# Revit family: NAU_Naughtone_Stng_Pullman1
name_source: partatom
category: Furniture
revit_build: Autodesk Revit 2018 (Build: 20170223_1515(x64)
units: mm (PartAtom-declared; Revit-internal decimal feet)

## family parameters
Always vertical = Yes
Cut with Voids When Loaded = No
OmniClass Number = 23.40.20.00
OmniClass Title = General Furniture and Specialties
Room Calculation Point = No
Shared = Yes
Work Plane-Based = No

## types (4) — shared parameters
AccessibilityPerformance = Table Top
Assembly Code = E2020200
AssetType = Movable
BIMObjectName = NAU_Naughtone_Seating_Pullman
Category = Pr_40_50_31 : Furniture booths
Color = Various
DurationUnit = year
Finish = Fabric upholstery
IfcExportAs = IfcFurnishingElementType
IfcExportType = BOOTH
Keynote = Pr_40_50_31
MainColor = Various
ManufacturerAddress = Knaresborough Tech Park, Manse Lane, Knaresborough, HG5 8LF
ManufacturerName = Naughtone
ManufacturerURL = www.naughtone.com
Material = Fabric, plywood frame, foam, steel/wooden legs, wooden table top
NBSDescription = Seating
NBSReference = 45-35-72/352
Name = Seating_Pullman_Naughtone
NominalHeight = 1300 mm  [stored 4.26509 ft]
ProductInformation = www.naughtone.com/products/pullman/
Revision = 1
Shape = Rectangular
SustainabilityPerformance = FSC certifeied, SCS indoor advantage gold
URL = www.naughtone.com
Uniclass2015Code = Pr_40_50_31
Uniclass2015Title = Furniture booths
Version = 1
WarrantyDescription = Request warranty information from naughtone
WarrantyDurationLabor = 7
WarrantyDurationParts = 7
WarrantyDurationUnit = year
zero-valued in all types: WorksurfaceArea

## per-type parameters (varying)
| type | CushionOffset | HasLargeTable | HasSmallTable | Model | ModelNumber | NominalLength | NominalWidth | NumberOfChairs | Size |
| Pullman 2 Seat Booth | 10 mm  [stored 0.0328084 ft] | No | Yes | PULB2H | PULB2H | 1300 mm  [stored 4.26509 ft] | 1950 mm  [stored 6.39764 ft] | 4 | 1950 x 1300 x 1300mm |
| Pullman 3 Seat Booth | 700 mm  [stored 2.29659 ft] | No | Yes | PULB3H | PULB3H | 1900 mm  [stored 6.2336 ft] | 1950 mm  [stored 6.39764 ft] | 6 | 1950 x 1900 x 1300mm |
| Pullman 3 Seat Booth Wide | 700 mm  [stored 2.29659 ft] | Yes | No | PULBW3H | PULBW3H | 1900 mm  [stored 6.2336 ft] | 2250 mm | 6 | 2250 x 1900 x 1300mm |
| Pullman 2 Seat Booth Wide | 10 mm  [stored 0.0328084 ft] | Yes | No | PULBW2H | PULBW2H | 1300 mm  [stored 4.26509 ft] | 2250 mm | 4 | 2250 x 1300 x 1300mm |

note: column(s) folded — value = type name in every type: Description, ModelReference

note: [stored X ft] marks values corroborated as IEEE doubles in the binary element streams (Revit-internal decimal feet)

## geometry (parser evidence)
native form markers: Sweep x5
no freeform markers — native parametric forms only
